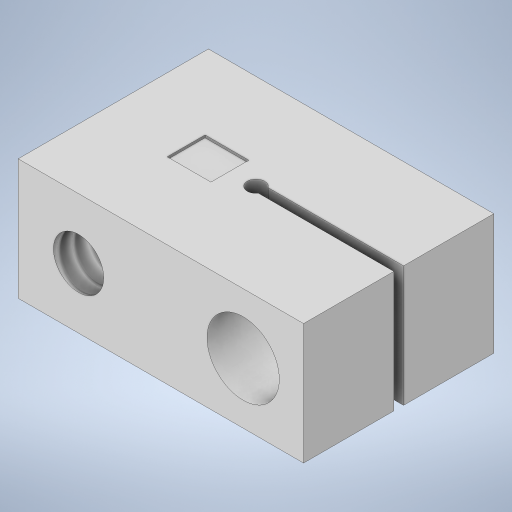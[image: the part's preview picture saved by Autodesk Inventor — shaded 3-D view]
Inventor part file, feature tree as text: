
AUTODESK INVENTOR PART (.ipt)
format: ipt  version: 2024 (Build 280153000, 153)  size: 292,352 bytes
history: native  units: in
note: dims shown in document units (in); Inventor stores cm internally (conversion verified against a paired STEP export)
features: sketch x6, extrude x3, hole x3, other x2
ambient origin geometry x8: Origin, YZ Plane, XZ Plane, XY Plane, X Axis, Y Axis, Z Axis, Center Point
bodies: Solid1 (feature_tree)
feature tree (14):
  other  "Annotations"
  extrude  "Extrusion1"  Depth=0.3937in
  sketch  "Sketch2"  dims[d2=0.2953in d3=0.036in]
  extrude  "Extrusion2"  Depth=0.036in
  hole  "Hole3"  [1 undecoded]
  hole  "Hole4"  [1 undecoded]
  hole  "Hole5"  [1 undecoded]
  sketch  "Sketch5"  dims[d9=0.138in d10=45.0deg]
  extrude  "Extrusion4"  Depth=0.3937in
  sketch  "Sketch1"  dims[d0=0.5906in d1=0.3937in]
  sketch  "Sketch3"  dims[d4=0.01in d5=0.01in]
  sketch  "Sketch4"  dims[d6=0.25in d7=0.0in d8=135.0deg]
  sketch  "Sketch6"  dims[d11=0.138in d30=0.04in d31=0.1378in d32=0.0in d35=0.104in d36=0.276in d37=0.375in d38=0.25in d39=0.5635in d40=1.0in d41=0.8108in d44=45.0deg d45=0.104in d46=0.104in d47=0.1969in d48=0.375in d49=0.25in d50=0.5635in d51=0.1969in d52=0.8108in d53=0.1495in d54=0.276in d55=0.279in d56=0.25in d57=0.5635in d58=0.1969in d59=0.8108in d60=0.3in d61=1.3in d62=0.25in d63=0.25in d64=0.25in d65=0.25in d66=1.451in d68=0.113in d69=0.113in d70=0.036in d79=0.0392in d80=0.0906in d81=0.0784in d82=0.005in d83=0.0in d84=0.3937in d42=1.8447in d43=0.104in]
  other  "Diameter Dimension 1"
note: 3 required parameter values undecoded (feature->parameter linkage not recoverable at this tier; creation-order binding heuristic only, values carry confidence <= 0.55)
